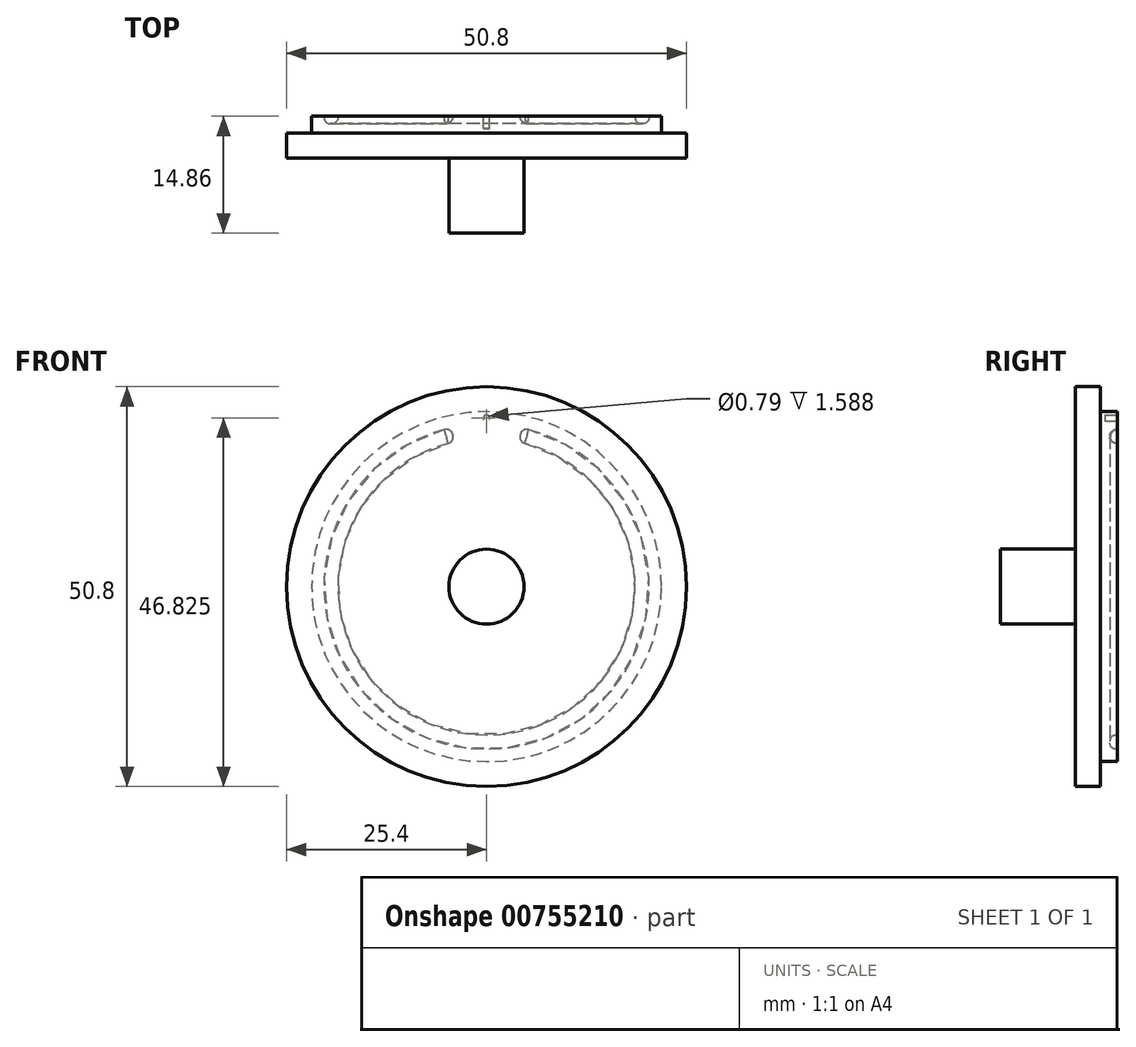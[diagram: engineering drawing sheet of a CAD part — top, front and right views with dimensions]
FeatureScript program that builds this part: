
annotation { "Feature Type Name" : "Feature", "Feature Type Description" : "" }
export const myFeature = defineFeature(function(context is Context, id is Id, definition is map)
    precondition{}
    {
        {
            var Q0;
            Q0=qCreatedBy(makeId("Front.planeOp"),FACE);
            var sketch = newSketch(context, id + "F0", { "sketchPlane" : qUnion([Q0])});
            skCircle(sketch, "E0", {"center": v(0, 0) * mm, "radius": 25.4 * mm});
            skSolve(sketch);
        }
        {
            var Q0;
            Q0 = qSketchRegion(id + "F0", true);
            extrude(context, id + "F1", {"entities" : qUnion([Q0]), "oppositeDirection" : true, "depth" : 3.17 * mm, "offsetDistance" : 25.4 * mm});
        }
        {
            var Q0;
            Q0=makeQuery(id+"F1.opExtrude","CAP_FACE",FACE,{"disambiguationData":[OSD([sQuery(id+"F0.wireOp",EDGE,"E0")])],"isStart":false});
            var sketch = newSketch(context, id + "F2", { "sketchPlane" : qUnion([Q0])});
            skCircle(sketch, "E1", {"center": v(0, 0) * mm, "radius": 22.23 * mm});
            skSolve(sketch);
        }
        {
            var Q0;
            Q0 = qSketchRegion(id + "F2", true);
            extrude(context, id + "F3", {"entities" : qUnion([Q0]), "operationType" : NewBodyOperationType.ADD, "depth" : 2.16 * mm, "offsetDistance" : 25.4 * mm});
        }
        {
            var Q0;
            Q0=makeQuery(id+"F3.opExtrude","CAP_FACE",FACE,{"disambiguationData":[OSD([sQuery(id+"F2.wireOp",EDGE,"E1")])],"isStart":false});
            var sketch = newSketch(context, id + "F4", { "sketchPlane" : qUnion([Q0])});
            skCircle(sketch, "E2", {"center": v(0, 21.42) * mm, "radius": 0.4 * mm});
            skSolve(sketch);
        }
        {
            var Q0;
            Q0 = qSketchRegion(id + "F4", true);
            extrude(context, id + "F5", {"entities" : qUnion([Q0]), "operationType" : NewBodyOperationType.REMOVE, "oppositeDirection" : true, "depth" : 1.59 * mm, "offsetDistance" : 25.4 * mm});
        }
        {
            var Q0;
            Q0=qCreatedBy(makeId("Right.planeOp"),FACE);
            var sketch = newSketch(context, id + "F6", { "sketchPlane" : qUnion([Q0])});
            skLineSegment(sketch, "E3", {"start": v(0, 0) * mm, "end": v(15.5, 0) * mm, "construction": true});
            skSolve(sketch);
        }
        {
            var Q0;
            Q0=qCreatedBy(makeId("Top.planeOp"),FACE);
            var Q1;
            Q1=sQuery(id+"F6.wireOp",EDGE,"E3");
            cPlane(context, id + "F7", {"entities" : qUnion([Q0, Q1]), "cplaneType" : CPlaneType.LINE_ANGLE, "offset" : 25.4 * mm, "angle" : 75 * degree, "width" : 152.4 * mm, "height" : 152.4 * mm});
        }
        {
            var Q0;
            Q0=qCreatedBy(id+"F7.planeOp",FACE);
            var sketch = newSketch(context, id + "F8", { "sketchPlane" : qUnion([Q0])});
            skLineSegment(sketch, "E4.bottom", {"start": v(-5.33, 20.65) * mm, "end": v(-5.19, 20.65) * mm});
            skLineSegment(sketch, "E4.top", {"start": v(-5.33, 18.86) * mm, "end": v(-5.19, 18.86) * mm});
            skLineSegment(sketch, "E4.left", {"start": v(-5.33, 20.65) * mm, "end": v(-5.33, 18.86) * mm});
            skLineSegment(sketch, "E4.right", {"start": v(-4.4, 19.86) * mm, "end": v(-4.4, 19.65) * mm});
            skPoint(sketch, "E5.visualSharp", {"position": v(-4.4, 20.65) * mm});
            skArc(sketch, "E5.filletArc", {"start": v(-4.4, 19.86) * mm, "mid": v(-4.63, 20.42) * mm, "end": v(-5.19, 20.65) * mm});
            skPoint(sketch, "E6.visualSharp", {"position": v(-4.4, 18.86) * mm});
            skArc(sketch, "E6.filletArc", {"start": v(-5.19, 18.86) * mm, "mid": v(-4.63, 19.1) * mm, "end": v(-4.4, 19.65) * mm});
            skSolve(sketch);
        }
        {
            var Q0;
            Q0 = qSketchRegion(id + "F8", true);
            var Q1;
            Q1=sQuery(id+"F6.wireOp",EDGE,"E3");
            revolve(context, id + "F9", {"operationType" : NewBodyOperationType.REMOVE, "surfaceOperationType" : NewSurfaceOperationType.NEW, "entities" : qUnion([Q0]), "axis" : qUnion([Q1]), "revolveType" : RevolveType.ONE_DIRECTION, "oppositeDirection" : true, "angle" : 330 * degree});
        }
        {
            var Q0;
            Q0=makeQuery(id+"F9.boolean.opBoolean","COPY",FACE,{"derivedFrom":makeQuery(id+"F9.opRevolve","CAP_FACE",FACE,{"disambiguationData":[OSD([sQuery(id+"F8.wireOp",EDGE,"E4.bottom"),sQuery(id+"F8.wireOp",EDGE,"E4.top"),sQuery(id+"F8.wireOp",EDGE,"E4.left"),sQuery(id+"F8.wireOp",EDGE,"E4.right"),sQuery(id+"F8.wireOp",EDGE,"E5.filletArc"),sQuery(id+"F8.wireOp",EDGE,"E6.filletArc")])],"isStart":false})});
            var sketch = newSketch(context, id + "F10", { "sketchPlane" : qUnion([Q0])});
            skLineSegment(sketch, "E7.bottom", {"start": v(5.33, 20.65) * mm, "end": v(5.26, 20.65) * mm});
            skLineSegment(sketch, "E7.top", {"start": v(5.33, 18.86) * mm, "end": v(5.26, 18.86) * mm});
            skLineSegment(sketch, "E7.left", {"start": v(5.33, 20.65) * mm, "end": v(5.33, 18.86) * mm});
            skLineSegment(sketch, "E7.right", {"start": v(4.47, 19.86) * mm, "end": v(4.47, 19.65) * mm});
            skPoint(sketch, "E8.visualSharp", {"position": v(4.47, 20.65) * mm});
            skArc(sketch, "E8.filletArc", {"start": v(5.26, 20.65) * mm, "mid": v(4.7, 20.42) * mm, "end": v(4.47, 19.86) * mm});
            skPoint(sketch, "E9.visualSharp", {"position": v(4.47, 18.86) * mm});
            skArc(sketch, "E9.filletArc", {"start": v(4.47, 19.65) * mm, "mid": v(4.7, 19.1) * mm, "end": v(5.26, 18.86) * mm});
            skSolve(sketch);
        }
        {
            var Q0;
            Q0 = qSketchRegion(id + "F10", true);
            var Q1;
            Q1=sQuery(id+"F10.wireOp",EDGE,"E7.left");
            revolve(context, id + "F11", {"operationType" : NewBodyOperationType.REMOVE, "surfaceOperationType" : NewSurfaceOperationType.NEW, "entities" : qUnion([Q0]), "axis" : qUnion([Q1]), "revolveType" : RevolveType.FULL, "oppositeDirection" : true});
        }
        {
            var Q0;
            Q0=makeQuery(id+"F9.boolean.opBoolean","COPY",FACE,{"derivedFrom":makeQuery(id+"F9.opRevolve","CAP_FACE",FACE,{"disambiguationData":[OSD([sQuery(id+"F8.wireOp",EDGE,"E4.bottom"),sQuery(id+"F8.wireOp",EDGE,"E4.top"),sQuery(id+"F8.wireOp",EDGE,"E4.left"),sQuery(id+"F8.wireOp",EDGE,"E4.right"),sQuery(id+"F8.wireOp",EDGE,"E5.filletArc"),sQuery(id+"F8.wireOp",EDGE,"E6.filletArc")])],"isStart":true})});
            var sketch = newSketch(context, id + "F12", { "sketchPlane" : qUnion([Q0])});
            skLineSegment(sketch, "E10.bottom", {"start": v(-5.33, 20.65) * mm, "end": v(-5.26, 20.65) * mm});
            skLineSegment(sketch, "E10.top", {"start": v(-5.33, 18.86) * mm, "end": v(-5.26, 18.86) * mm});
            skLineSegment(sketch, "E10.left", {"start": v(-5.33, 20.65) * mm, "end": v(-5.33, 18.86) * mm});
            skLineSegment(sketch, "E10.right", {"start": v(-4.47, 19.86) * mm, "end": v(-4.47, 19.65) * mm});
            skPoint(sketch, "E11.visualSharp", {"position": v(-4.47, 20.65) * mm});
            skArc(sketch, "E11.filletArc", {"start": v(-4.47, 19.86) * mm, "mid": v(-4.7, 20.42) * mm, "end": v(-5.26, 20.65) * mm});
            skPoint(sketch, "E12.visualSharp", {"position": v(-4.47, 18.86) * mm});
            skArc(sketch, "E12.filletArc", {"start": v(-5.26, 18.86) * mm, "mid": v(-4.7, 19.1) * mm, "end": v(-4.47, 19.65) * mm});
            skSolve(sketch);
        }
        {
            var Q0;
            Q0 = qSketchRegion(id + "F12", true);
            var Q1;
            Q1=sQuery(id+"F12.wireOp",EDGE,"E10.left");
            revolve(context, id + "F13", {"operationType" : NewBodyOperationType.REMOVE, "surfaceOperationType" : NewSurfaceOperationType.NEW, "entities" : qUnion([Q0]), "axis" : qUnion([Q1]), "revolveType" : RevolveType.FULL, "oppositeDirection" : true});
        }
        {
            var Q0;
            Q0=makeQuery(id+"F1.opExtrude","CAP_FACE",FACE,{"disambiguationData":[OSD([sQuery(id+"F0.wireOp",EDGE,"E0")])],"isStart":true});
            var sketch = newSketch(context, id + "F14", { "sketchPlane" : qUnion([Q0])});
            skCircle(sketch, "E13", {"center": v(0, 0) * mm, "radius": 4.76 * mm});
            skSolve(sketch);
        }
        {
            var Q0;
            Q0 = qSketchRegion(id + "F14", true);
            extrude(context, id + "F15", {"entities" : qUnion([Q0]), "operationType" : NewBodyOperationType.ADD, "depth" : 9.52 * mm, "offsetDistance" : 25.4 * mm});
        }
    });
